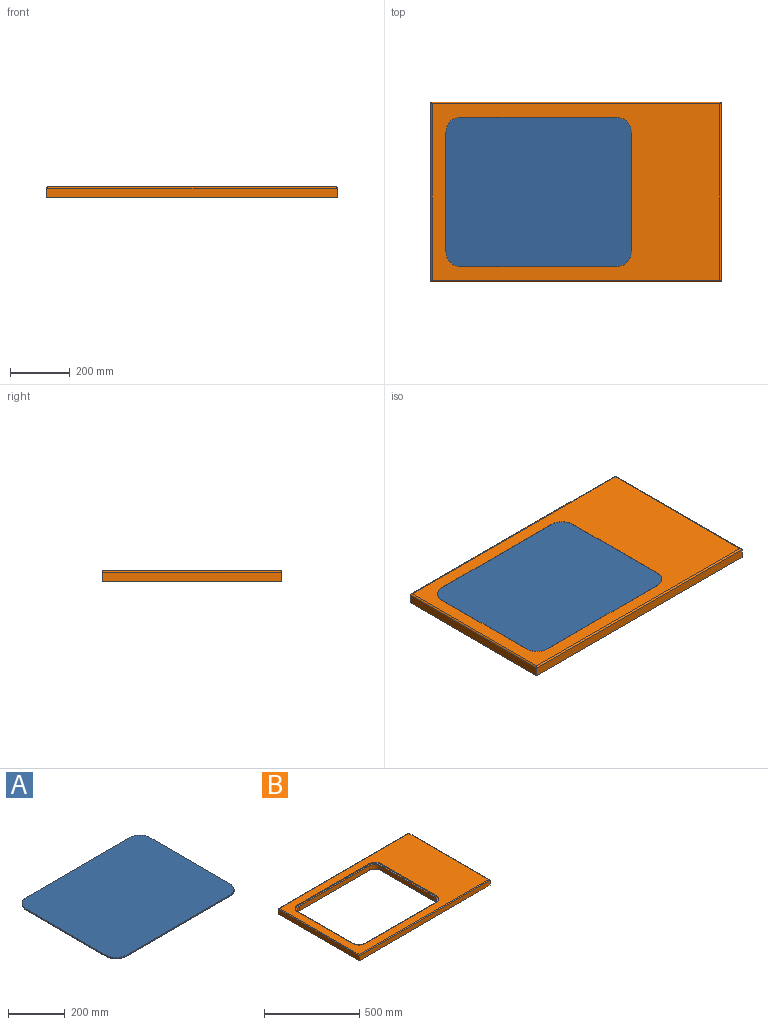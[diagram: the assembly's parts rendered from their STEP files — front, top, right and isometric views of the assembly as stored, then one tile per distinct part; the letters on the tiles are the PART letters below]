
ASSEMBLY  parts=2 mates=1
PART A: 10 faces, bbox 620x500x5 mm
  f0: plane 520x5mm, normal (0,1,0), area 2600mm2, adj f1,f7,f8,f9
  f1: cylinder r=50mm len=50mm, axis (0,0,-1), area 392.7mm2, adj f0,f2,f8,f9
  f2: plane 400x5mm, normal (-1,0,0), area 2000mm2, adj f1,f3,f8,f9
  f3: cylinder r=50mm len=50mm, axis (0,0,-1), area 392.7mm2, adj f2,f4,f8,f9
  f4: plane 520x5mm, normal (0,-1,0), area 2600mm2, adj f3,f5,f8,f9
  f5: cylinder r=50mm len=50mm, axis (0,0,-1), area 392.7mm2, adj f4,f6,f8,f9
  f6: plane 400x5mm, normal (1,0,0), area 2000mm2, adj f5,f7,f8,f9
  f7: cylinder r=50mm len=50mm, axis (0,0,-1), area 392.7mm2, adj f0,f6,f8,f9
  f8: plane 620x500mm, normal (0,0,1), area 307854mm2, adj f0,f1,f2,f3,f4,f5,f6,f7
  f9: plane 620x500mm, normal (0,0,-1), area 307854mm2, adj f0,f1,f2,f3,f4,f5,f6,f7
PART B: 27 faces, bbox 970x600x36 mm
  f0: plane 620x500mm, normal (0,0,1), area 21227.5mm2, adj f6,f7,f8,f9,f10,f11,f12,f13
  f1: plane 970x31mm, normal (0,1,0), area 30070mm2, adj f2,f4,f5,f24
  f2: plane 600x31mm, normal (-1,0,0), area 18600mm2, adj f1,f3,f5,f23
  f3: plane 970x31mm, normal (0,-1,0), area 30070mm2, adj f2,f4,f5,f25
  f4: plane 600x31mm, normal (1,0,0), area 18600mm2, adj f1,f3,f5,f26
  f5: plane 970x600mm, normal (0,0,-1), area 295373.5mm2, adj f1,f2,f3,f4,f6,f7,f8,f9
  f6: cylinder r=40mm len=40mm, axis (0,0,1), area 1885mm2, adj f0,f5,f7,f13
  f7: plane 520x30mm, normal (0,1,0), area 15600mm2, adj f0,f5,f6,f8
  f8: cylinder r=40mm len=40mm, axis (0,0,1), area 1885mm2, adj f0,f5,f7,f9
  f9: plane 400x30mm, normal (-1,0,0), area 12000mm2, adj f0,f5,f8,f10
  f10: cylinder r=40mm len=40mm, axis (0,0,1), area 1885mm2, adj f0,f5,f9,f11
  f11: plane 520x30mm, normal (0,-1,0), area 15600mm2, adj f0,f5,f10,f12
  f12: cylinder r=40mm len=40mm, axis (0,0,1), area 1885mm2, adj f0,f5,f11,f13
  f13: plane 400x30mm, normal (1,0,0), area 12000mm2, adj f0,f5,f6,f12
  f14: cylinder r=50mm len=50mm, axis (0,0,-1), area 471.2mm2, adj f0,f15,f21,f22
  f15: plane 520x6mm, normal (0,-1,0), area 3120mm2, adj f0,f14,f16,f22
  f16: cylinder r=50mm len=50mm, axis (0,0,-1), area 471.2mm2, adj f0,f15,f17,f22
  f17: plane 400x6mm, normal (-1,0,0), area 2400mm2, adj f0,f16,f18,f22
  f18: cylinder r=50mm len=50mm, axis (0,0,-1), area 471.2mm2, adj f0,f17,f19,f22
  f19: plane 520x6mm, normal (0,1,0), area 3120mm2, adj f0,f18,f20,f22
  f20: cylinder r=50mm len=50mm, axis (0,0,-1), area 471.2mm2, adj f0,f19,f21,f22
  f21: plane 400x6mm, normal (1,0,0), area 2400mm2, adj f0,f14,f20,f22
  f22: plane 960x590mm, normal (0,0,1), area 258546mm2, adj f14,f15,f16,f17,f18,f19,f20,f21
  f23: cylinder r=5mm len=600mm, axis (0,1,0), area 4683.8mm2, adj f2,f22,f24,f25
  f24: cylinder r=5mm len=970mm, axis (1,0,0), area 7589.8mm2, adj f1,f22,f23,f26
  f25: cylinder r=5mm len=970mm, axis (-1,0,0), area 7589.8mm2, adj f3,f22,f23,f26
  f26: cylinder r=5mm len=600mm, axis (0,-1,0), area 4683.8mm2, adj f4,f22,f24,f25
PLACE A at identity
PLACE B at identity
MATE fastened A.f4 <-> B.f19  axis (0,-1,0) through (-38.93,-262.66,30)mm
